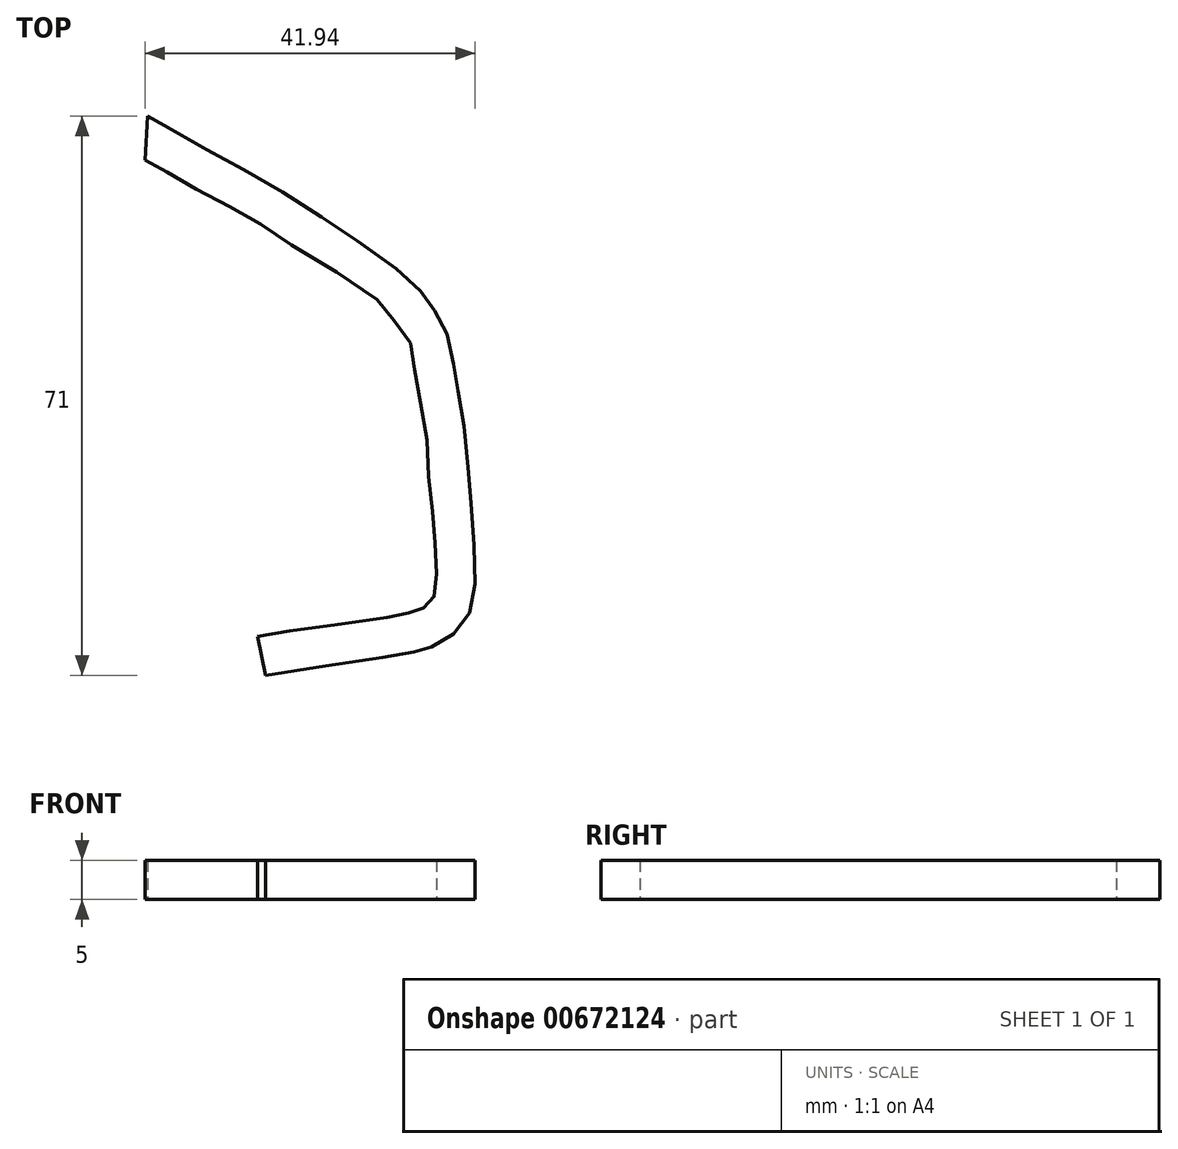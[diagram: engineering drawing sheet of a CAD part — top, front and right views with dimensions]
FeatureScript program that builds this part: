
annotation { "Feature Type Name" : "Feature", "Feature Type Description" : "" }
export const myFeature = defineFeature(function(context is Context, id is Id, definition is map)
    precondition{}
    {
        {
            var Q0;
            Q0=qCreatedBy(makeId("Top.planeOp"),FACE);
            var sketch = newSketch(context, id + "F0", { "sketchPlane" : qUnion([Q0])});
            skLineSegment(sketch, "E0", {"start": v(-4.6, 33.67) * mm, "end": v(-6.13, -29.81) * mm, "construction": true});
            skFitSpline(sketch, "E1", {"points": [v(-4.6, 33.67) * mm, v(3.18, 29.3) * mm, v(8.78, 26.19) * mm, v(14.89, 22.32) * mm, v(24.9, 15.41) * mm, v(27.24, 12.86) * mm, v(28.98, 9.95) * mm, v(29.75, 6.33) * mm, v(30.82, 0) * mm, v(31.48, -6.63) * mm, v(32.01, -12.44) * mm, v(32.29, -17.27) * mm, v(32.23, -21.07) * mm, v(31.79, -22.21) * mm, v(31, -23.02) * mm, v(30.15, -23.47) * mm, v(28.91, -23.85) * mm, v(27.17, -24.22) * mm, v(9.7, -26.9) * mm], "startDerivative": vector(103.33, -58.46) * mm, "endDerivative": vector(-164.62, -26.73) * mm});
            skFitSpline(sketch, "E2.0", {"points": [v(-2.14, 38.02) * mm, v(-1.06, 37.41) * mm, v(0.57, 36.5) * mm, v(2.69, 35.3) * mm, v(3.98, 34.58) * mm, v(4.98, 34.03) * mm, v(5.95, 33.5) * mm, v(7.6, 32.6) * mm, v(9.4, 31.6) * mm, v(10.97, 30.7) * mm, v(11.86, 30.17) * mm, v(13.18, 29.37) * mm, v(14.72, 28.39) * mm, v(16.47, 27.26) * mm, v(17.55, 26.55) * mm, v(18.43, 25.98) * mm, v(19.35, 25.38) * mm, v(20.63, 24.54) * mm, v(22.29, 23.45) * mm, v(24.25, 22.12) * mm, v(25.79, 21.04) * mm, v(26.91, 20.2) * mm, v(27.7, 19.59) * mm, v(28.44, 18.97) * mm, v(29.1, 18.37) * mm, v(29.7, 17.77) * mm, v(30.22, 17.18) * mm, v(30.6, 16.72) * mm, v(30.87, 16.37) * mm, v(31.06, 16.12) * mm, v(31.23, 15.88) * mm, v(31.45, 15.58) * mm, v(31.75, 15.16) * mm, v(32.14, 14.6) * mm, v(32.54, 13.95) * mm, v(32.89, 13.36) * mm, v(33.15, 12.85) * mm, v(33.35, 12.45) * mm, v(33.54, 12.02) * mm, v(33.72, 11.57) * mm, v(33.87, 11.12) * mm, v(34.05, 10.55) * mm, v(34.22, 9.86) * mm, v(34.42, 8.85) * mm, v(34.54, 8.07) * mm, v(34.63, 7.46) * mm, v(34.67, 7.17) * mm, v(34.72, 6.87) * mm, v(34.8, 6.45) * mm, v(34.89, 5.9) * mm, v(35.06, 4.94) * mm, v(35.25, 3.9) * mm, v(35.44, 2.8) * mm, v(35.58, 1.96) * mm, v(35.71, 1.1) * mm, v(35.88, -0.07) * mm, v(36.04, -1.5) * mm, v(36.2, -3.14) * mm, v(36.32, -4.45) * mm, v(36.4, -5.48) * mm, v(36.47, -6.22) * mm, v(36.53, -6.96) * mm, v(36.62, -7.95) * mm, v(36.74, -9.18) * mm, v(36.88, -10.64) * mm, v(37, -12.1) * mm, v(37.1, -13.52) * mm, v(37.19, -14.9) * mm, v(37.26, -16.27) * mm, v(37.3, -17.64) * mm, v(37.34, -18.86) * mm, v(37.33, -19.84) * mm, v(37.3, -20.58) * mm, v(37.26, -21.22) * mm, v(37.19, -21.77) * mm, v(37.08, -22.36) * mm, v(36.88, -23.15) * mm, v(36.55, -23.96) * mm, v(36.23, -24.55) * mm, v(35.99, -24.94) * mm, v(35.75, -25.27) * mm, v(35.43, -25.68) * mm, v(35, -26.15) * mm, v(34.55, -26.58) * mm, v(34.15, -26.9) * mm, v(33.72, -27.23) * mm, v(33.13, -27.6) * mm, v(32.57, -27.88) * mm, v(32.17, -28.05) * mm, v(31.9, -28.15) * mm, v(31.64, -28.24) * mm, v(31.32, -28.35) * mm, v(31.02, -28.45) * mm, v(30.73, -28.54) * mm, v(30.52, -28.6) * mm, v(30.32, -28.65) * mm, v(30.14, -28.7) * mm, v(29.94, -28.75) * mm, v(29.65, -28.83) * mm, v(29.25, -28.92) * mm, v(28.73, -29.02) * mm, v(28.12, -29.13) * mm, v(27.38, -29.25) * mm, v(26.2, -29.44) * mm, v(24.4, -29.72) * mm, v(21.82, -30.1) * mm, v(18.99, -30.52) * mm, v(15.06, -31.1) * mm, v(12.18, -31.55) * mm, v(10.5, -31.83) * mm]});
            skLineSegment(sketch, "E3", {"start": v(-5.8, -31.17) * mm, "end": v(-3.84, -40.84) * mm, "construction": true});
            skLineSegment(sketch, "E4", {"start": v(10.68, -31.8) * mm, "end": v(9.7, -26.9) * mm});
            skLineSegment(sketch, "E5", {"start": v(-4.6, 33.67) * mm, "end": v(-4.26, 39.2) * mm});
            skLineSegment(sketch, "E6", {"start": v(-2.14, 38.02) * mm, "end": v(-4.26, 39.2) * mm});
            skSolve(sketch);
        }
        {
            var Q0;
            Q0=qCreatedBy(makeId("Top.planeOp"),FACE);
            var sketch = newSketch(context, id + "F1", { "sketchPlane" : qUnion([Q0])});
            skFitSpline(sketch, "E7.0", {"points": [v(-4.6, 33.67) * mm, v(-1.95, 32.17) * mm, v(3.08, 29.33) * mm, v(8.98, 26.18) * mm, v(14.65, 22.46) * mm, v(25.09, 15.72) * mm, v(27.15, 13.03) * mm, v(29.3, 9.94) * mm, v(29.68, 6.22) * mm, v(30.98, -0.1) * mm, v(31.44, -6.55) * mm, v(32.05, -12.4) * mm, v(32.3, -17.03) * mm, v(32.4, -21.02) * mm, v(31.88, -22.2) * mm, v(31.02, -23.08) * mm, v(30.17, -23.5) * mm, v(28.76, -23.9) * mm, v(26.98, -24.33) * mm, v(15.64, -25.93) * mm, v(9.7, -26.9) * mm]});
            skFitSpline(sketch, "E7.1", {"points": [v(-2.14, 38.02) * mm, v(-1.06, 37.41) * mm, v(0.57, 36.5) * mm, v(2.69, 35.3) * mm, v(3.98, 34.58) * mm, v(4.98, 34.03) * mm, v(5.95, 33.5) * mm, v(7.6, 32.6) * mm, v(9.4, 31.6) * mm, v(10.97, 30.7) * mm, v(11.86, 30.17) * mm, v(13.18, 29.37) * mm, v(14.72, 28.39) * mm, v(16.47, 27.26) * mm, v(17.55, 26.55) * mm, v(18.43, 25.98) * mm, v(19.35, 25.38) * mm, v(20.63, 24.54) * mm, v(22.29, 23.45) * mm, v(24.25, 22.12) * mm, v(25.79, 21.04) * mm, v(26.91, 20.2) * mm, v(27.7, 19.59) * mm, v(28.44, 18.97) * mm, v(29.1, 18.37) * mm, v(29.7, 17.77) * mm, v(30.22, 17.18) * mm, v(30.6, 16.72) * mm, v(30.87, 16.37) * mm, v(31.06, 16.12) * mm, v(31.23, 15.88) * mm, v(31.45, 15.58) * mm, v(31.75, 15.16) * mm, v(32.14, 14.6) * mm, v(32.54, 13.95) * mm, v(32.89, 13.36) * mm, v(33.15, 12.85) * mm, v(33.35, 12.45) * mm, v(33.54, 12.02) * mm, v(33.72, 11.57) * mm, v(33.87, 11.12) * mm, v(34.05, 10.55) * mm, v(34.22, 9.86) * mm, v(34.42, 8.85) * mm, v(34.54, 8.07) * mm, v(34.63, 7.46) * mm, v(34.67, 7.17) * mm, v(34.72, 6.87) * mm, v(34.8, 6.45) * mm, v(34.89, 5.9) * mm, v(35.06, 4.94) * mm, v(35.25, 3.9) * mm, v(35.44, 2.8) * mm, v(35.58, 1.96) * mm, v(35.71, 1.1) * mm, v(35.88, -0.07) * mm, v(36.04, -1.5) * mm, v(36.2, -3.14) * mm, v(36.32, -4.45) * mm, v(36.4, -5.48) * mm, v(36.47, -6.22) * mm, v(36.53, -6.96) * mm, v(36.62, -7.95) * mm, v(36.74, -9.18) * mm, v(36.88, -10.64) * mm, v(37, -12.1) * mm, v(37.1, -13.52) * mm, v(37.19, -14.9) * mm, v(37.26, -16.27) * mm, v(37.3, -17.64) * mm, v(37.34, -18.86) * mm, v(37.33, -19.84) * mm, v(37.3, -20.58) * mm, v(37.26, -21.22) * mm, v(37.19, -21.77) * mm, v(37.08, -22.36) * mm, v(36.88, -23.15) * mm, v(36.55, -23.96) * mm, v(36.23, -24.55) * mm, v(35.99, -24.94) * mm, v(35.75, -25.27) * mm, v(35.43, -25.68) * mm, v(35, -26.15) * mm, v(34.55, -26.58) * mm, v(34.15, -26.9) * mm, v(33.72, -27.23) * mm, v(33.13, -27.6) * mm, v(32.57, -27.88) * mm, v(32.17, -28.05) * mm, v(31.9, -28.15) * mm, v(31.64, -28.24) * mm, v(31.32, -28.35) * mm, v(31.02, -28.45) * mm, v(30.73, -28.54) * mm, v(30.52, -28.6) * mm, v(30.32, -28.65) * mm, v(30.14, -28.7) * mm, v(29.94, -28.75) * mm, v(29.65, -28.83) * mm, v(29.25, -28.92) * mm, v(28.73, -29.02) * mm, v(28.12, -29.13) * mm, v(27.38, -29.25) * mm, v(26.2, -29.44) * mm, v(24.4, -29.72) * mm, v(21.82, -30.1) * mm, v(18.99, -30.52) * mm, v(15.06, -31.1) * mm, v(12.18, -31.55) * mm, v(10.5, -31.83) * mm]});
            skPoint(sketch, "E7.2", {"position": v(-4.26, 39.2) * mm});
            skLineSegment(sketch, "E7.3", {"start": v(-4.6, 33.67) * mm, "end": v(-4.26, 39.2) * mm});
            skLineSegment(sketch, "E7.4", {"start": v(-2.14, 38.02) * mm, "end": v(-4.26, 39.2) * mm});
            skLineSegment(sketch, "E7.5", {"start": v(10.68, -31.8) * mm, "end": v(9.7, -26.9) * mm});
            skSolve(sketch);
        }
        {
            var Q0;
            Q0 = qSketchRegion(id + "F1", true);
            extrude(context, id + "F2", {"entities" : qUnion([Q0]), "depth" : 5 * mm, "offsetDistance" : 25 * mm});
        }
    });
